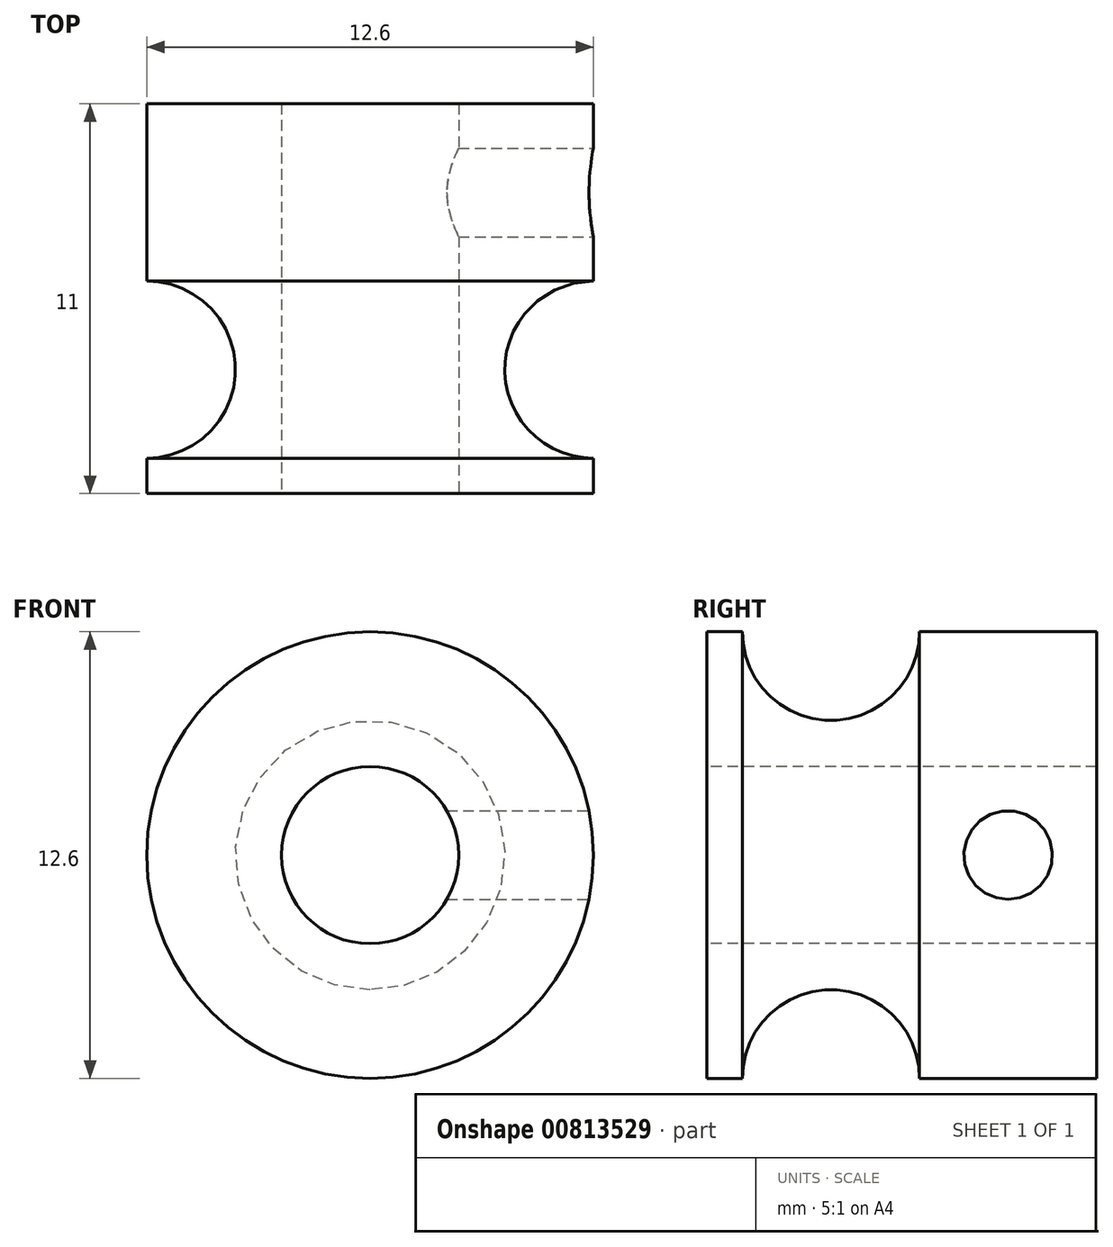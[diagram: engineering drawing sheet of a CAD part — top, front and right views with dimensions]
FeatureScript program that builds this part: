
annotation { "Feature Type Name" : "Feature", "Feature Type Description" : "" }
export const myFeature = defineFeature(function(context is Context, id is Id, definition is map)
    precondition{}
    {
        {
            var Q0;
            Q0=qCreatedBy(makeId("Front.planeOp"),FACE);
            var sketch = newSketch(context, id + "F0", { "sketchPlane" : qUnion([Q0])});
            skCircle(sketch, "E0", {"center": v(0, 0) * mm, "radius": 6.3 * mm});
            skCircle(sketch, "E1", {"center": v(0, 0) * mm, "radius": 5.2 * mm, "construction": true});
            skCircle(sketch, "E2", {"center": v(0, 0) * mm, "radius": 2.5 * mm});
            skSolve(sketch);
        }
        {
            var Q0;
            Q0=makeQuery(id+"F0.imprint","IMPRINT",FACE,{"disambiguationData":[TD([[makeQuery(id+"F0.imprint","IMPRINT",EDGE,{"derivedFrom":sQuery(id+"F0.wireOp",EDGE,"E0")}),1.0]])]});
            extrude(context, id + "F1", {"entities" : qUnion([Q0]), "oppositeDirection" : true, "depth" : 5 * mm, "offsetDistance" : 25 * mm, "hasSecondDirection" : true, "secondDirectionOppositeDirection" : false, "secondDirectionDepth" : 6 * mm});
        }
        {
            var Q0;
            Q0=qCreatedBy(makeId("Right.planeOp"),FACE);
            var sketch = newSketch(context, id + "F2", { "sketchPlane" : qUnion([Q0])});
            skLineSegment(sketch, "E3", {"start": v(-6, 6.3) * mm, "end": v(5, 6.3) * mm});
            skCircle(sketch, "E4", {"center": v(-2.5, 6.3) * mm, "radius": 2.5 * mm});
            skPoint(sketch, "E5", {"position": v(2.5, 0) * mm});
            skSolve(sketch);
        }
        {
            var Q0;
            {var subQ0=sQuery(id+"F2.wireOp",EDGE,"E4");var subQ1=sQuery(id+"F2.wireOp",EDGE,"E3");var subQ2=makeQuery(id+"F2.imprint","INTERSECT",VERTEX,{"disambiguationData":[OD(0.0)],"derivedFrom":[subQ1,subQ0]});Q0=makeQuery(id+"F2.imprint","IMPRINT",FACE,{"disambiguationData":[TD([[makeQuery(id+"F2.imprint","IMPRINT",EDGE,{"disambiguationData":[TD([[subQ2,-1.0]])],"derivedFrom":subQ1}),1.0]])]});}
            var Q1;
            {var subQ0=sQuery(id+"F2.wireOp",EDGE,"E4");var subQ1=sQuery(id+"F2.wireOp",EDGE,"E3");var subQ2=makeQuery(id+"F2.imprint","INTERSECT",VERTEX,{"disambiguationData":[OD(0.0)],"derivedFrom":[subQ1,subQ0]});Q1=makeQuery(id+"F2.imprint","IMPRINT",FACE,{"disambiguationData":[TD([[makeQuery(id+"F2.imprint","IMPRINT",EDGE,{"disambiguationData":[TD([[subQ2,-1.0]])],"derivedFrom":subQ1}),-1.0]])]});}
            var Q2;
            Q2=makeQuery(id+"F1.opExtrude","CAP_EDGE",EDGE,{"disambiguationData":[OSD([sQuery(id+"F0.wireOp",EDGE,"E0")])],"isStart":true});
            revolve(context, id + "F3", {"operationType" : NewBodyOperationType.REMOVE, "surfaceOperationType" : NewSurfaceOperationType.NEW, "entities" : qUnion([Q0, Q1]), "axis" : qUnion([Q2]), "revolveType" : RevolveType.FULL, "oppositeDirection" : true});
        }
        {
            var Q0;
            Q0=qCreatedBy(makeId("Right.planeOp"),FACE);
            cPlane(context, id + "F4", {"entities" : qUnion([Q0]), "cplaneType" : CPlaneType.OFFSET, "offset" : (12.6 / 2) * mm, "width" : 150 * mm, "height" : 150 * mm});
        }
        {
            var Q0;
            Q0=qCreatedBy(id+"F4.planeOp",FACE);
            var sketch = newSketch(context, id + "F5", { "sketchPlane" : qUnion([Q0])});
            skPoint(sketch, "E6", {"position": v(2.5, 0) * mm});
            skSolve(sketch);
        }
        {
            var Q0;
            Q0=sQuery(id+"F5.wireOp",VERTEX,"E6");
            var Q1;
            Q1=makeQuery(id+"F1.opExtrude","SWEPT_BODY",BODY,{"disambiguationData":[OSD([sQuery(id+"F0.wireOp",EDGE,"E0"),sQuery(id+"F0.wireOp",EDGE,"E2")])]});
            hole(context, id + "F6", {"style" : HoleStyle.SIMPLE, "endStyle" : HoleEndStyle.BLIND, "holeDiameter" : 2.5 * mm, "majorDiameter" : 5 * mm, "holeDepth" : 5 * mm, "isTappedThrough" : true, "tappedDepth" : 12 * mm, "tapClearance" : 3, "locations" : qUnion([Q0]), "scope" : qUnion([Q1])});
        }
    });
